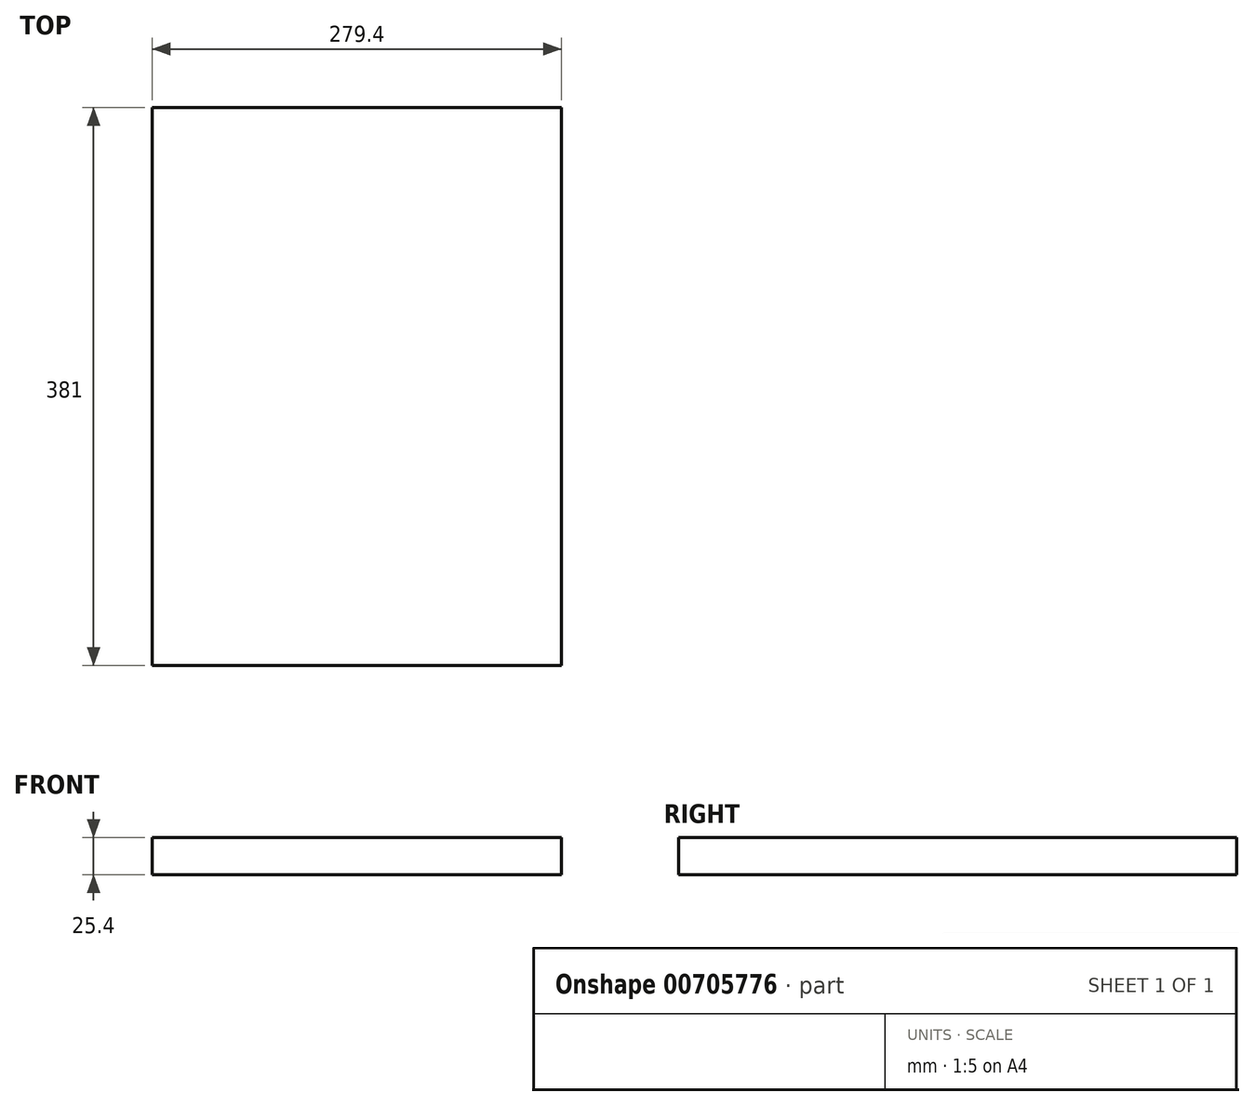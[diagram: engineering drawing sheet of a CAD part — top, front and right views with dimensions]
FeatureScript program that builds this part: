
annotation { "Feature Type Name" : "Feature", "Feature Type Description" : "" }
export const myFeature = defineFeature(function(context is Context, id is Id, definition is map)
    precondition{}
    {
        {
            var Q0;
            Q0=qCreatedBy(makeId("Front.planeOp"),FACE);
            var sketch = newSketch(context, id + "F0", { "sketchPlane" : qUnion([Q0])});
            skLineSegment(sketch, "E0.bottom", {"start": v(-139.7, 12.7) * mm, "end": v(139.7, 12.7) * mm});
            skLineSegment(sketch, "E0.top", {"start": v(-139.7, -12.7) * mm, "end": v(139.7, -12.7) * mm});
            skLineSegment(sketch, "E0.left", {"start": v(-139.7, 12.7) * mm, "end": v(-139.7, -12.7) * mm});
            skLineSegment(sketch, "E0.right", {"start": v(139.7, 12.7) * mm, "end": v(139.7, -12.7) * mm});
            skPoint(sketch, "E0.middle", {"position": v(0, 0) * mm});
            skSolve(sketch);
        }
        {
            var Q0;
            Q0 = qSketchRegion(id + "F0", true);
            extrude(context, id + "F1", {"entities" : qUnion([Q0]), "depth" : 381 * mm, "offsetDistance" : 25.4 * mm});
        }
    });
